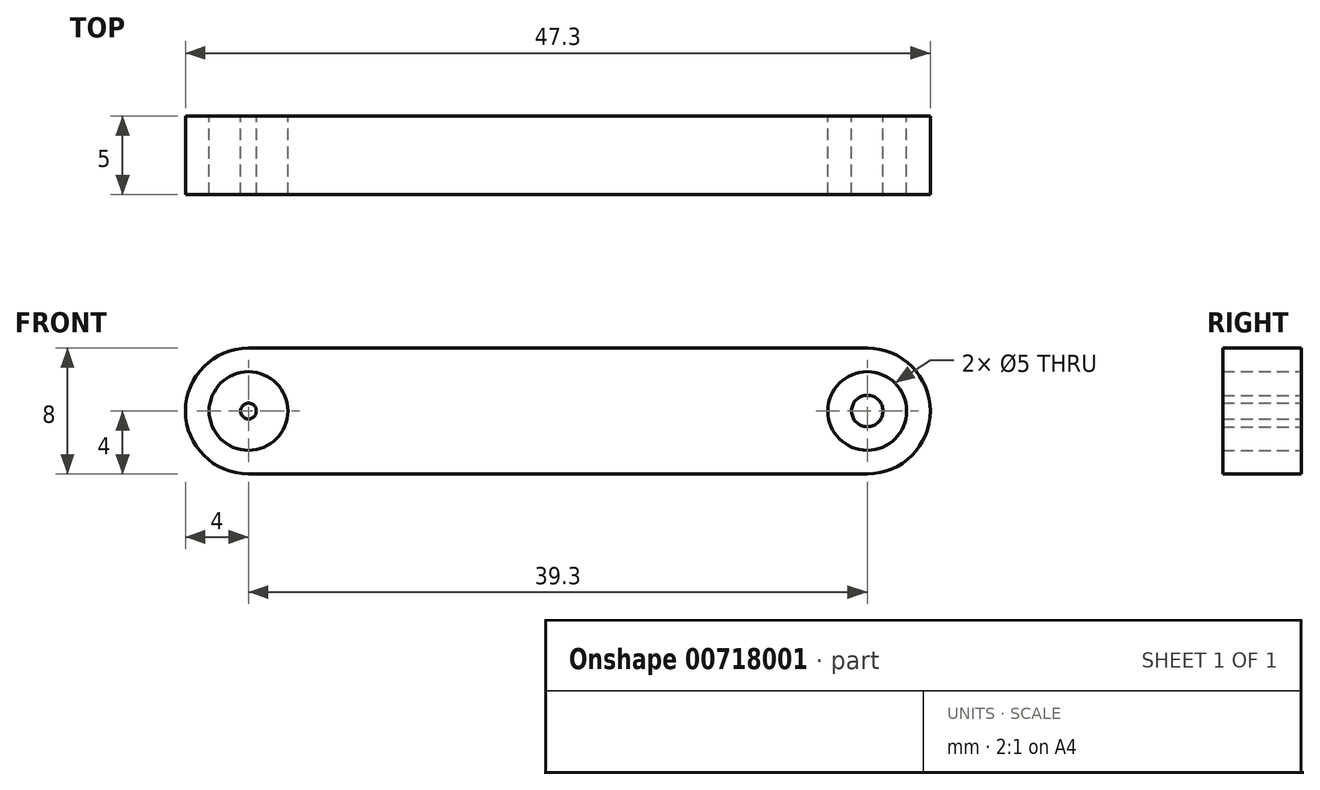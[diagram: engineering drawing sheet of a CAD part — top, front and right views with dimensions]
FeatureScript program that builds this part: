
annotation { "Feature Type Name" : "Feature", "Feature Type Description" : "" }
export const myFeature = defineFeature(function(context is Context, id is Id, definition is map)
    precondition{}
    {
        {
            var Q0;
            Q0=qCreatedBy(makeId("Front.planeOp"),FACE);
            var sketch = newSketch(context, id + "F0", { "sketchPlane" : qUnion([Q0])});
            skCircle(sketch, "E0", {"center": v(0, 0) * mm, "radius": 4 * mm});
            skCircle(sketch, "E1", {"center": v(39.3, 0) * mm, "radius": 4 * mm});
            skLineSegment(sketch, "E2", {"start": v(0, -4) * mm, "end": v(39.3, -4) * mm});
            skLineSegment(sketch, "E3", {"start": v(0, 4) * mm, "end": v(39.3, 4) * mm});
            skCircle(sketch, "E4", {"center": v(39.3, 0) * mm, "radius": 2.5 * mm});
            skCircle(sketch, "E5", {"center": v(0, 0) * mm, "radius": 2.5 * mm});
            skCircle(sketch, "E6", {"center": v(0, 0) * mm, "radius": 0.5 * mm});
            skCircle(sketch, "E7", {"center": v(39.3, 0) * mm, "radius": 1 * mm});
            skSolve(sketch);
        }
        {
            var Q0;
            Q0 = qSketchRegion(id + "F0", true);
            var Q1;
            Q1=makeQuery(id+"F0.imprint","IMPRINT",FACE,{"disambiguationData":[TD([[makeQuery(id+"F0.imprint","IMPRINT",EDGE,{"derivedFrom":sQuery(id+"F0.wireOp",EDGE,"E6")}),1.0]])]});
            var Q2;
            Q2=makeQuery(id+"F0.imprint","IMPRINT",FACE,{"disambiguationData":[TD([[makeQuery(id+"F0.imprint","IMPRINT",EDGE,{"derivedFrom":sQuery(id+"F0.wireOp",EDGE,"E7")}),1.0]])]});
            extrude(context, id + "F1", {"entities" : qUnion([Q0, Q1, Q2]), "depth" : 5 * mm, "offsetDistance" : 25 * mm});
        }
    });
